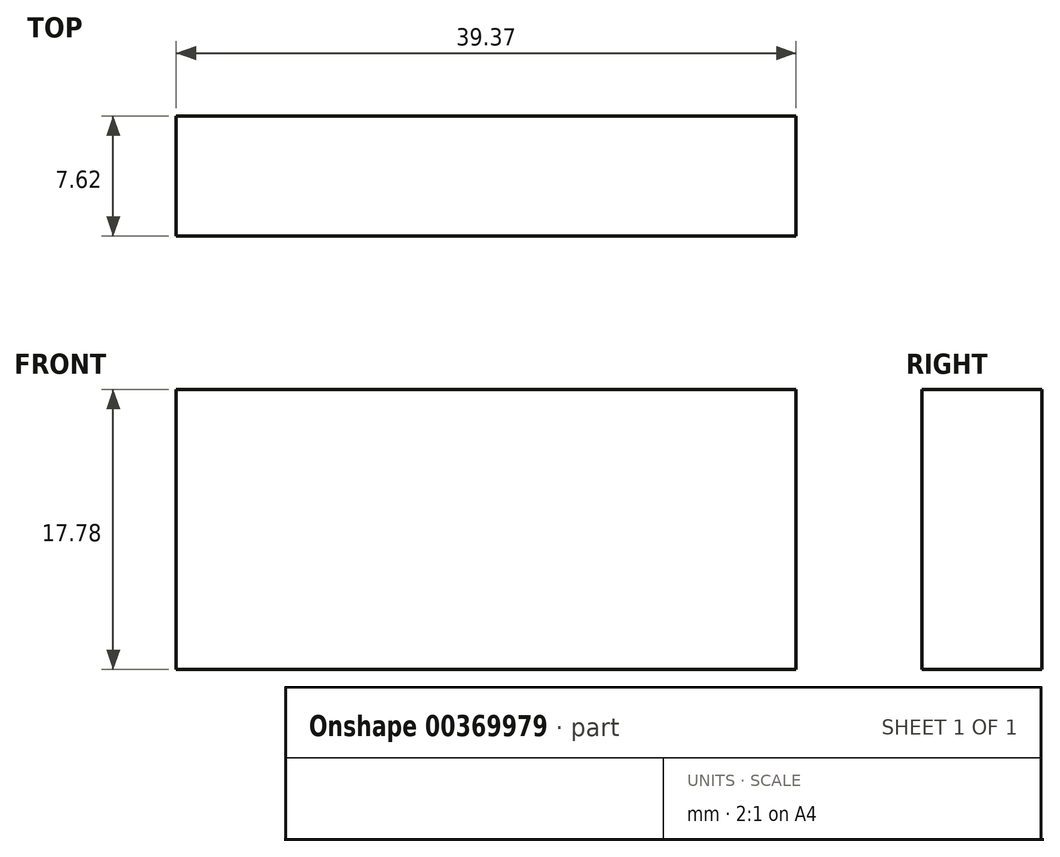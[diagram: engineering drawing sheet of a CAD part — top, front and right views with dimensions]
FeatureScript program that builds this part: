
annotation { "Feature Type Name" : "Feature", "Feature Type Description" : "" }
export const myFeature = defineFeature(function(context is Context, id is Id, definition is map)
    precondition{}
    {
        {
            var Q0;
            Q0=qCreatedBy(makeId("Front.planeOp"),FACE);
            var sketch = newSketch(context, id + "F0", { "sketchPlane" : qUnion([Q0])});
            skLineSegment(sketch, "E0.bottom", {"start": v(-85.5, -68.5) * mm, "end": v(-46.12, -68.5) * mm});
            skLineSegment(sketch, "E0.top", {"start": v(-85.5, -50.72) * mm, "end": v(-46.12, -50.72) * mm});
            skLineSegment(sketch, "E0.left", {"start": v(-85.5, -68.5) * mm, "end": v(-85.5, -50.72) * mm});
            skLineSegment(sketch, "E0.right", {"start": v(-46.12, -68.5) * mm, "end": v(-46.12, -50.72) * mm});
            skPoint(sketch, "E1.firstSnap0", {"position": v(-85.5, -59.61) * mm});
            skSolve(sketch);
        }
        {
            var Q0;
            Q0 = qSketchRegion(id + "F0", true);
            extrude(context, id + "F1", {"entities" : qUnion([Q0]), "depth" : 7.62 * mm});
        }
    });
